# Revit family: Grohe_PlumbingFixture_UnisetElement_WC_39688000
name_source: partatom
category: Plumbing Fixtures
revit_build: Autodesk Revit 2018 (Build: 20190510_1515(x64)
units: mm (PartAtom-declared; Revit-internal decimal feet)

## family parameters
Cut with Voids When Loaded = No
Host = Face
OmniClass Number = 23.65.00.00
OmniClass Title = Supply and Distribution of Liquids and Gases
Part Type = Normal
Room Calculation Point = No
Round Connector Dimension = Use Diameter
Shared = No

## types (1)
- 39688000
    Assembly Code = C1030110
    AssetType = Fixed
    BIMObjectName = Grohe_PlumbingFixture_UnisetElement_WC_39688000
    ClassificationName = Uniclass2015
    ClassificationValue = Pr_40_20_93_89
    Cost = 0 $
    Default Elevation = 0 mm  [stored 0 ft]
    Description = Slim tank fits standard 2” x 4” stud walls. Dual flush – 0.8gpf and 1.6gpf (3L and 6L). Low noise operation – meets strict European
noise (DIN) standards. No tools required for the installation of the
inspection shaft including protection during
construction phase, for vertical use. Self-supporting, pre-assembled powder coated steel frame with quick and lockable adjustments. ADA Compliant, bowl rim height adjustment from 15” to 19”. Pneumatic discharge valve offering 3 modes of operation: dual flush, start/stop or single flush. Tank insulated to prevent condensation. 2 fixing bolts included, 7- 9in (180-230mm) mounting screw distance ½” water supply connection from top, integrated angle valve. Actuation plate sold separately. TÜV approved for load capacity 44” (1.13m) installation height. CALGreen compliant. WaterSense® compliant when paired with listed WaterSense® high efficiency compatible
    DurationUnit = Years
    ExpectedLife = 0
    IfcExportAs = IfcSanitaryTerminalType
    IfcExportType = CISTERN
    Keynote = N13
    Manufacturer = Grohe
    ManufacturerName = Grohe
    ModelNumber = 39688000
    NBSDescription = WC cisterns
    NBSObjectName = Grohe - WC cisterns
    NBSReference = 45-35-70/383
    NominalDepth = 0 mm  [stored 0 ft]
    NominalHeight = 0 mm  [stored 0 ft]
    NominalLength = 0 mm  [stored 0 ft]
    ProductionYear = 2021
    ReplacementCost = 0
    Type Comments = 39688000
    TypeName = 39688000
    URL = https://www.grohe.us
    WarrantyDurationLabor = 0
    WarrantyDurationParts = 0
    WarrantyDurationUnit = Years
    _BSBibleVersion = 16
    _BimSpecGuid = 0
    _CurrentRevision = 1
    _DistributedBy = www.bimstore.co

note: [stored X ft] marks values corroborated as IEEE doubles in the binary element streams (Revit-internal decimal feet)

## geometry (parser evidence)
native form markers: Sweep x2
no freeform markers — native parametric forms only
